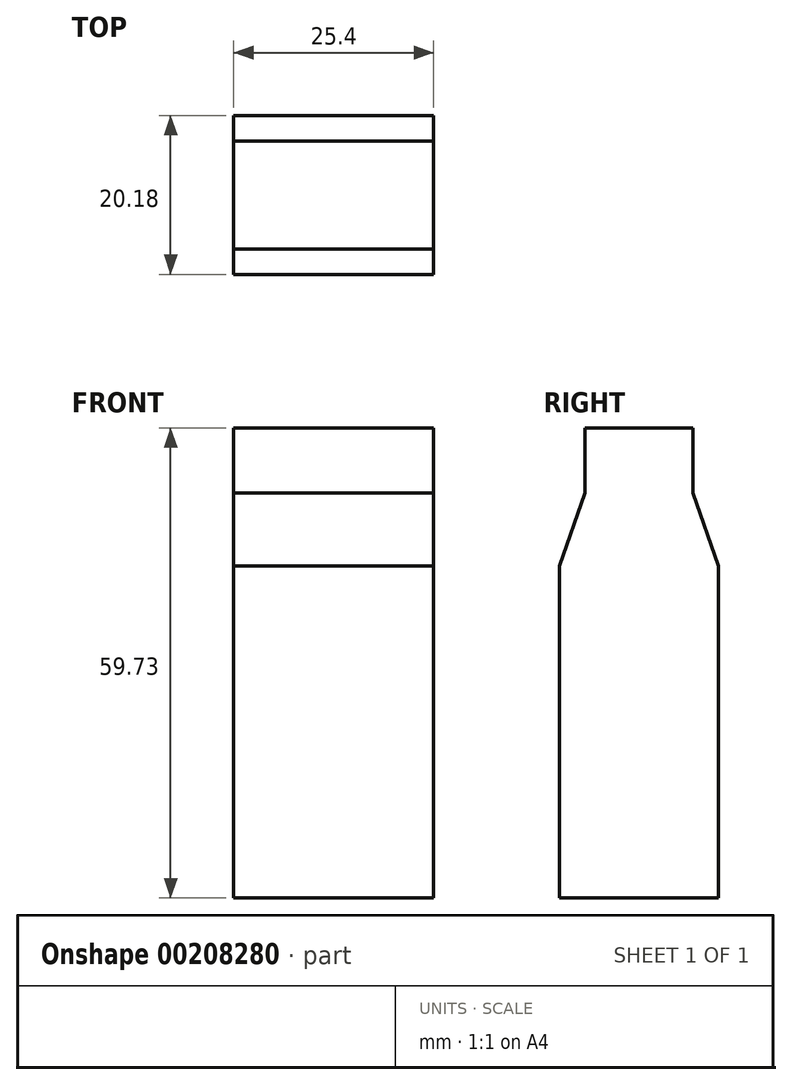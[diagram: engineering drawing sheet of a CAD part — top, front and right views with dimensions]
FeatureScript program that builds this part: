
annotation { "Feature Type Name" : "Feature", "Feature Type Description" : "" }
export const myFeature = defineFeature(function(context is Context, id is Id, definition is map)
    precondition{}
    {
        {
            var Q0;
            Q0=qCreatedBy(makeId("Right.planeOp"),FACE);
            var sketch = newSketch(context, id + "F0", { "sketchPlane" : qUnion([Q0])});
            skLineSegment(sketch, "E0.top", {"start": v(-10.09, -21.09) * mm, "end": v(10.09, -21.09) * mm});
            skLineSegment(sketch, "E0.left", {"start": v(-10.09, 21.09) * mm, "end": v(-10.09, -21.09) * mm});
            skLineSegment(sketch, "E0.right", {"start": v(10.09, 21.09) * mm, "end": v(10.09, -21.09) * mm});
            skPoint(sketch, "E0.middle", {"position": v(0, 0) * mm});
            skLineSegment(sketch, "E1", {"start": v(-10.09, 21.09) * mm, "end": v(-6.86, 30.37) * mm});
            skLineSegment(sketch, "E2", {"start": v(-6.86, 30.37) * mm, "end": v(-6.86, 38.64) * mm});
            skLineSegment(sketch, "E3", {"start": v(-6.86, 38.64) * mm, "end": v(0, 38.64) * mm});
            skLineSegment(sketch, "E4.MirrorCS", {"start": v(6.86, 38.64) * mm, "end": v(0, 38.64) * mm});
            skLineSegment(sketch, "E5.MirrorCS", {"start": v(6.86, 30.37) * mm, "end": v(6.86, 38.64) * mm});
            skLineSegment(sketch, "E6.MirrorCS", {"start": v(10.09, 21.09) * mm, "end": v(6.86, 30.37) * mm});
            skSolve(sketch);
        }
        {
            var Q0;
            Q0=makeQuery(id+"F0.imprint","IMPRINT",FACE,{"disambiguationData":[TD([[makeQuery(id+"F0.imprint","IMPRINT",EDGE,{"derivedFrom":sQuery(id+"F0.wireOp",EDGE,"E0.top")}),1.0]])]});
            extrude(context, id + "F1", {"entities" : qUnion([Q0]), "endBound" : BoundingType.SYMMETRIC, "depth" : 25.4 * mm});
        }
    });
